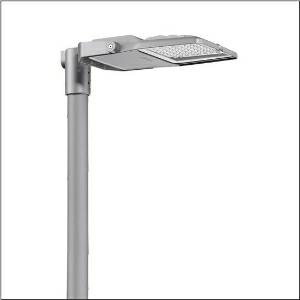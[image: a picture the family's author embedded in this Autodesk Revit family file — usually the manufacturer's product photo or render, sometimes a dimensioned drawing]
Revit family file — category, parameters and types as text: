
# Revit family: floodlight_fl_21_iq_mini___pl61_5xa7772d2c3a_9c70
name_source: partatom
category: Lighting Fixtures
units: mm (PartAtom-declared; Revit-internal decimal feet)

## family parameters
Cut with Voids When Loaded = No
Host = Face
Light Source = No
Part Type = Normal
Room Calculation Point = No
Round Connector Dimension = Use Diameter
Shared = No

## types (1)
- --- (1 x LED, 17500 lm, 143 W, 3000K)
    Apparent Load = 143 VA
    CIE Flux Codes = 33 65 98 100 100
    Color Rendering = 70
    Color Temperature = 3000K
    Default Elevation = 1800 mm
    Description = Floodlight FL 21 iQ mini, floodlight, primary light control with lens, of PMMA, primary optical cover: protective disc, of toughened safety glass, transparent, light distribution: PL61, light emission: direct distribution, installation type: surface-mounted, lamps: LED, High Power LED, rated values: 17.500lm | 143W | 122,4lm/W (begin service life); end service life: 17.500lm | 151,6W; at 50% lumin. flux: 8.750lm | 60,6W | 144,4lm/W, colour temperature: 3000K, colour rendering: CRI > 70, light colour: 730, light setting 1 begin service life: 100% | 17.500lm | 143W | 122,4lm/W | 3.000K, light setting 1 end service life: 151,6W, further light settings possible, control: pre-setting: linear dimming characteristic, Auto-Match, Temp-Guard, Night-Set, Smart-Wire, Desk-Remote (wireless, voltage-free reading and setting of iQ features in the workshop via application-optimized NFC function/RFID function), optimised constant luminous flux control (CLO 2.0), Light-Fading, Lumen-Switch, with terminal, 6-pole, mains connection: 220..240V, AC, 50/60Hz, luminaire housing, of diecast aluminium, powder-coated, SITECO metallic grey (DB 702S), corrosivity category C5 mid according to DIN EN ISO 12944suitable for swimming poolschlorine-resistant, sealing non-destructively replaceable, please order mast flange separately, mast bracket, of steel, galvanised, powder-coated, protection rating (complete): IP66, insulation class (complete): insulation class II (safety insulation), certification: CE, ENEC, VDE, protection symbol: D, impact resistance: IK08, permissible operating ambient temperature: -40..+40°C, permissible operating ambient temperature for outdoor applications: -40..+50°C, standard: DIN EN 12944, LABS conformity tested according to VDMA 24364:2018-05, packaging unit: 1 piece

Light Distribution: PL61
    Height = 70 mm
    Lamp = 1 x LED
    Lamp Light Flux = 17500 lm
    Lamp Power = 143 W
    Lamp count = 1
    Length = 485 mm
    Luminous efficacy = 122 lm/W
    Manufacturer = Siteco
    ModVariant = No
    Model = 5XA7772D2C3A
    Number of Poles = 1
    OnlyDefault = Yes
    Power Factor = 1
    Product Name = Floodlight FL 21 iQ mini | PL61
    Product group = floodlight | pylon annexe
    ProductGroupID = 6201
    Protection Class = Protection class II
    Protection Degree = IP 66
    RLX_Detail_Level = 1
    RLX_Emergency_Light_Flux = 0 lm
    RLX_Emergency_Type = 0
    RLX_Emergency_Type_DB = No
    RlxData = <blob elided: 101845 chars, md5=4a3ac8a2>
    Socket = socket
    Standby Power = 0 W
    System Light Flux = 17500 lm
    System Power = 143 W
    Type Comments = factory setting: luminous flux: 100 % | dim-lin: 254 | 730 mA
    Type Image = l_1007125.jpg
    URL = http://relux.com
    VarID = @adj_171937
    Voltage = 0 V
    Weight = 0.00 kg
    Width = 337 mm

## geometry (parser evidence)
native form markers: Blend x4, Sweep x14
no freeform markers — native parametric forms only
